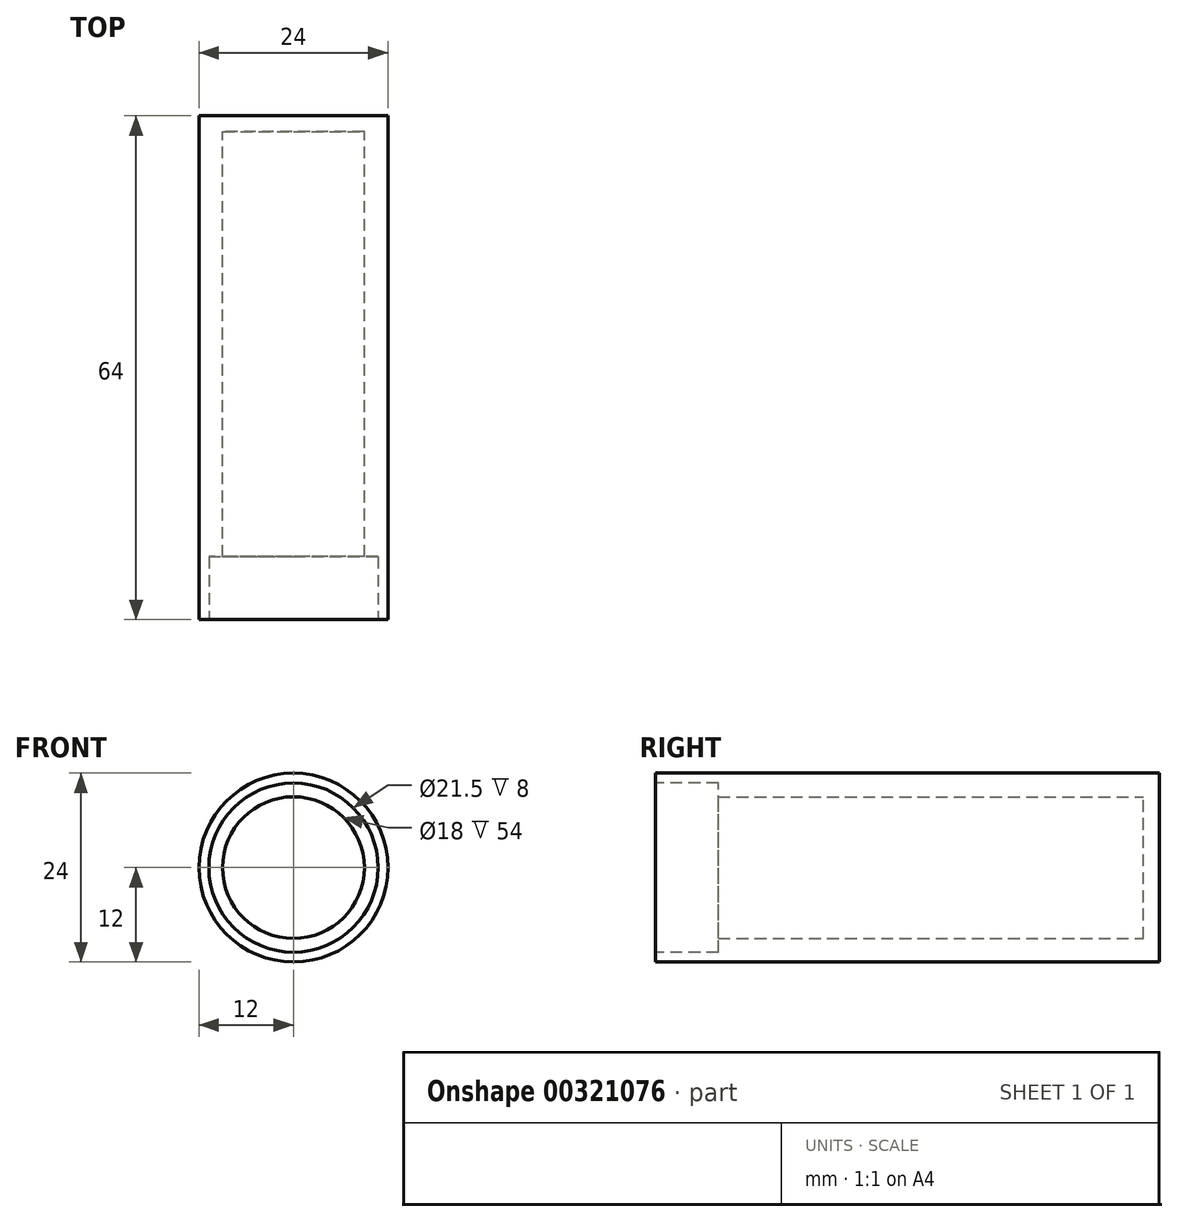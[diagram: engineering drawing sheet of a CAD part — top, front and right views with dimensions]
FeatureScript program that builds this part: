
annotation { "Feature Type Name" : "Feature", "Feature Type Description" : "" }
export const myFeature = defineFeature(function(context is Context, id is Id, definition is map)
    precondition{}
    {
        {
            var Q0;
            Q0=qCreatedBy(makeId("Front.planeOp"),FACE);
            var sketch = newSketch(context, id + "F0", { "sketchPlane" : qUnion([Q0])});
            skCircle(sketch, "E0", {"center": v(0, 0) * mm, "radius": 9 * mm});
            skCircle(sketch, "E1", {"center": v(0, 0) * mm, "radius": 12 * mm});
            skSolve(sketch);
        }
        {
            var Q0;
            Q0 = qSketchRegion(id + "F0", true);
            extrude(context, id + "F1", {"entities" : qUnion([Q0]), "depth" : 62 * mm});
        }
        {
            var Q0;
            Q0=makeQuery(id+"F1.opExtrude","CAP_FACE",FACE,{"disambiguationData":[OSD([sQuery(id+"F0.wireOp",EDGE,"E0"),sQuery(id+"F0.wireOp",EDGE,"E1")])],"isStart":true});
            var sketch = newSketch(context, id + "F2", { "sketchPlane" : qUnion([Q0])});
            skCircle(sketch, "E2", {"center": v(0, 0) * mm, "radius": 12 * mm});
            skSolve(sketch);
        }
        {
            var Q0;
            Q0 = qSketchRegion(id + "F2", true);
            extrude(context, id + "F3", {"entities" : qUnion([Q0]), "operationType" : NewBodyOperationType.ADD, "depth" : 2 * mm});
        }
        {
            var Q0;
            Q0=makeQuery(id+"F1.opExtrude","CAP_FACE",FACE,{"disambiguationData":[OSD([sQuery(id+"F0.wireOp",EDGE,"E0"),sQuery(id+"F0.wireOp",EDGE,"E1")])],"isStart":false});
            var sketch = newSketch(context, id + "F4", { "sketchPlane" : qUnion([Q0])});
            skCircle(sketch, "E3", {"center": v(0, 0) * mm, "radius": 10.75 * mm});
            skSolve(sketch);
        }
        {
            var Q0;
            Q0 = qSketchRegion(id + "F4", true);
            extrude(context, id + "F5", {"entities" : qUnion([Q0]), "operationType" : NewBodyOperationType.REMOVE, "oppositeDirection" : true, "depth" : 8 * mm});
        }
    });
